# Revit family: Toilet-Floor_Mount-KOHLER-Harken-K-22695T_1
name_source: partatom
category: Plumbing Fixtures
units: mm (PartAtom-declared; Revit-internal decimal feet)

## family parameters
Cut with Voids When Loaded = No
Host = Face
OmniClass Number = 23.31.19.00
OmniClass Title = Toilets
Part Type = Normal
Room Calculation Point = No
Round Connector Dimension = Use Diameter
Shared = No

## types (4) — shared parameters
ADA Compliant = No
Assembly Code = D2010100
Bowl Height = 15 9/16"
CW Connection = Yes
Cold Water Inlet = Cold Water Inlet
Date Modified = 09/07/2022
Default Elevation = 0"
Description = 0NE PIECE TOILET 305 MM
Flow Rate = 0 GPM
HW Connection = No
Height = 26 13/16"
Hot Water Inlet = Hot Water Inlet
Length = 28 7/8"
Manufacturer = Kohler Co.
Master Format 2014 = 22 42 13.13
Master Format 2014 Name = Residential Water Closets
Material = Vitreous China
Pressure = 0.00 psi
Product Name = Harken
Rough-In = 12"
Seat Included = Yes
URL = http://www.kohler.com.cn
Vent Connection = No
Waste Connection = Yes
Waste Water Outlet = Waste Water Outlet
WaterSense Certified = No
Width = 15 11/16"

## per-type parameters (varying)
| type | Finish | Flush Rate- GPF | Flush Rate- LPF | Model | Product Documentation Link | Product Page URL | Type |
| 4.8 LPF, 0-White | Kohler-Vitreous_China-0-White | 1.27 GPF | 4.8 LPF | K-22695T-S-0 | https://files.kohler.com.cn | https://www.kohler.com.cn | 1 |
| 4.5 LPF, 0-White | Kohler-Vitreous_China-0-White | 1.19 GPF | 4.5 LPF | K-22695T-SW-0 |  |  | 3 |
| 4.8 LPF, TRF-Truffle | KOHLER-Vitreous_China-TRF-Truffle | 1.27 GPF | 4.8 LPF | K-22695T-S-TRF | https://files.kohler.com.cn | https://www.kohler.com.cn | 2 |
| 4.5 LPF, TRF-Truffle | KOHLER-Vitreous_China-TRF-Truffle | 1.19 GPF | 4.5 LPF | K-22695T-SW-TRF |  |  | 4 |

## geometry (parser evidence)
native form markers: Sweep x3
no freeform markers — native parametric forms only
